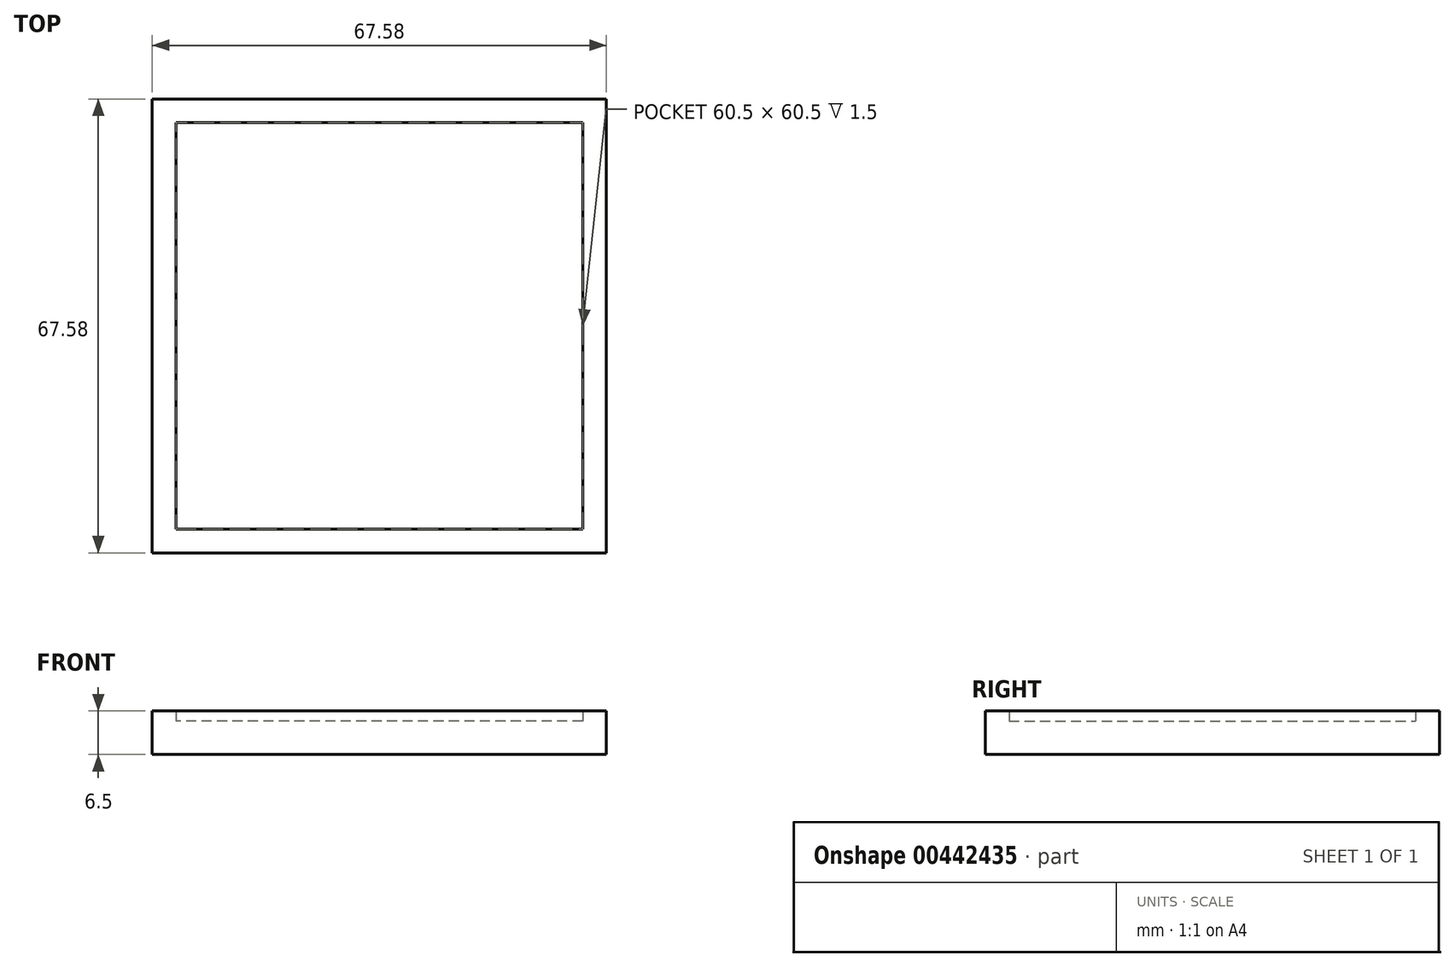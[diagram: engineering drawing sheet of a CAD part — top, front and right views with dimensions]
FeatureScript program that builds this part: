
annotation { "Feature Type Name" : "Feature", "Feature Type Description" : "" }
export const myFeature = defineFeature(function(context is Context, id is Id, definition is map)
    precondition{}
    {
        {
            var Q0;
            Q0=qCreatedBy(makeId("Top.planeOp"),FACE);
            var sketch = newSketch(context, id + "F0", { "sketchPlane" : qUnion([Q0])});
            skLineSegment(sketch, "E0.bottom", {"start": v(-60.5, 30.25) * mm, "end": v(0, 30.25) * mm});
            skLineSegment(sketch, "E0.top", {"start": v(-60.5, -30.25) * mm, "end": v(0, -30.25) * mm});
            skLineSegment(sketch, "E0.left", {"start": v(-60.5, 30.25) * mm, "end": v(-60.5, -30.25) * mm});
            skLineSegment(sketch, "E0.right", {"start": v(0, 30.25) * mm, "end": v(0, -30.25) * mm});
            skLineSegment(sketch, "E1.bottom", {"start": v(100, 20) * mm, "end": v(120, 20) * mm});
            skLineSegment(sketch, "E1.top", {"start": v(100, -20) * mm, "end": v(120, -20) * mm});
            skLineSegment(sketch, "E1.left", {"start": v(100, 20) * mm, "end": v(100, -20) * mm});
            skLineSegment(sketch, "E1.right", {"start": v(120, 20) * mm, "end": v(120, -20) * mm});
            skCircle(sketch, "E2", {"center": v(110, 0) * mm, "radius": 2.5 * mm});
            skLineSegment(sketch, "E3", {"start": v(110, 0) * mm, "end": v(110, 20) * mm, "construction": true});
            skPoint(sketch, "E3.endSnap0", {"position": v(110, 20) * mm});
            skLineSegment(sketch, "E4", {"start": v(110, 0) * mm, "end": v(120, 0) * mm, "construction": true});
            skLineSegment(sketch, "E5.bottom", {"start": v(-64.04, 33.79) * mm, "end": v(3.54, 33.79) * mm});
            skLineSegment(sketch, "E5.top", {"start": v(-64.04, -33.79) * mm, "end": v(3.54, -33.79) * mm});
            skLineSegment(sketch, "E5.left", {"start": v(-64.04, 33.79) * mm, "end": v(-64.04, -33.79) * mm});
            skLineSegment(sketch, "E5.right", {"start": v(3.54, 33.79) * mm, "end": v(3.54, -33.79) * mm});
            skLineSegment(sketch, "E6.bottom", {"start": v(100, 12.5) * mm, "end": v(3.54, 12.5) * mm});
            skLineSegment(sketch, "E6.top", {"start": v(100, -12.5) * mm, "end": v(3.54, -12.5) * mm});
            skLineSegment(sketch, "E6.left", {"start": v(100, 12.5) * mm, "end": v(100, -12.5) * mm});
            skLineSegment(sketch, "E6.right", {"start": v(3.54, 12.5) * mm, "end": v(3.54, -12.5) * mm});
            skLineSegment(sketch, "E7", {"start": v(3.54, 0) * mm, "end": v(0, 0) * mm, "construction": true});
            skSolve(sketch);
        }
        {
            var Q0;
            Q0=makeQuery(id+"F0.imprint","IMPRINT",FACE,{"disambiguationData":[TD([[makeQuery(id+"F0.imprint","IMPRINT",EDGE,{"derivedFrom":sQuery(id+"F0.wireOp",EDGE,"E0.bottom")}),-1.0]])]});
            var Q1;
            Q1=makeQuery(id+"F0.imprint","IMPRINT",FACE,{"disambiguationData":[TD([[makeQuery(id+"F0.imprint","IMPRINT",EDGE,{"derivedFrom":sQuery(id+"F0.wireOp",EDGE,"E0.bottom")}),1.0]])]});
            extrude(context, id + "F1", {"entities" : qUnion([Q0, Q1]), "depth" : 5 * mm});
        }
        {
            var Q0;
            Q0=makeQuery(id+"F0.imprint","IMPRINT",FACE,{"disambiguationData":[TD([[makeQuery(id+"F0.imprint","IMPRINT",EDGE,{"derivedFrom":sQuery(id+"F0.wireOp",EDGE,"E0.bottom")}),1.0]])]});
            extrude(context, id + "F2", {"entities" : qUnion([Q0]), "operationType" : NewBodyOperationType.ADD, "depth" : 6.5 * mm});
        }
    });
